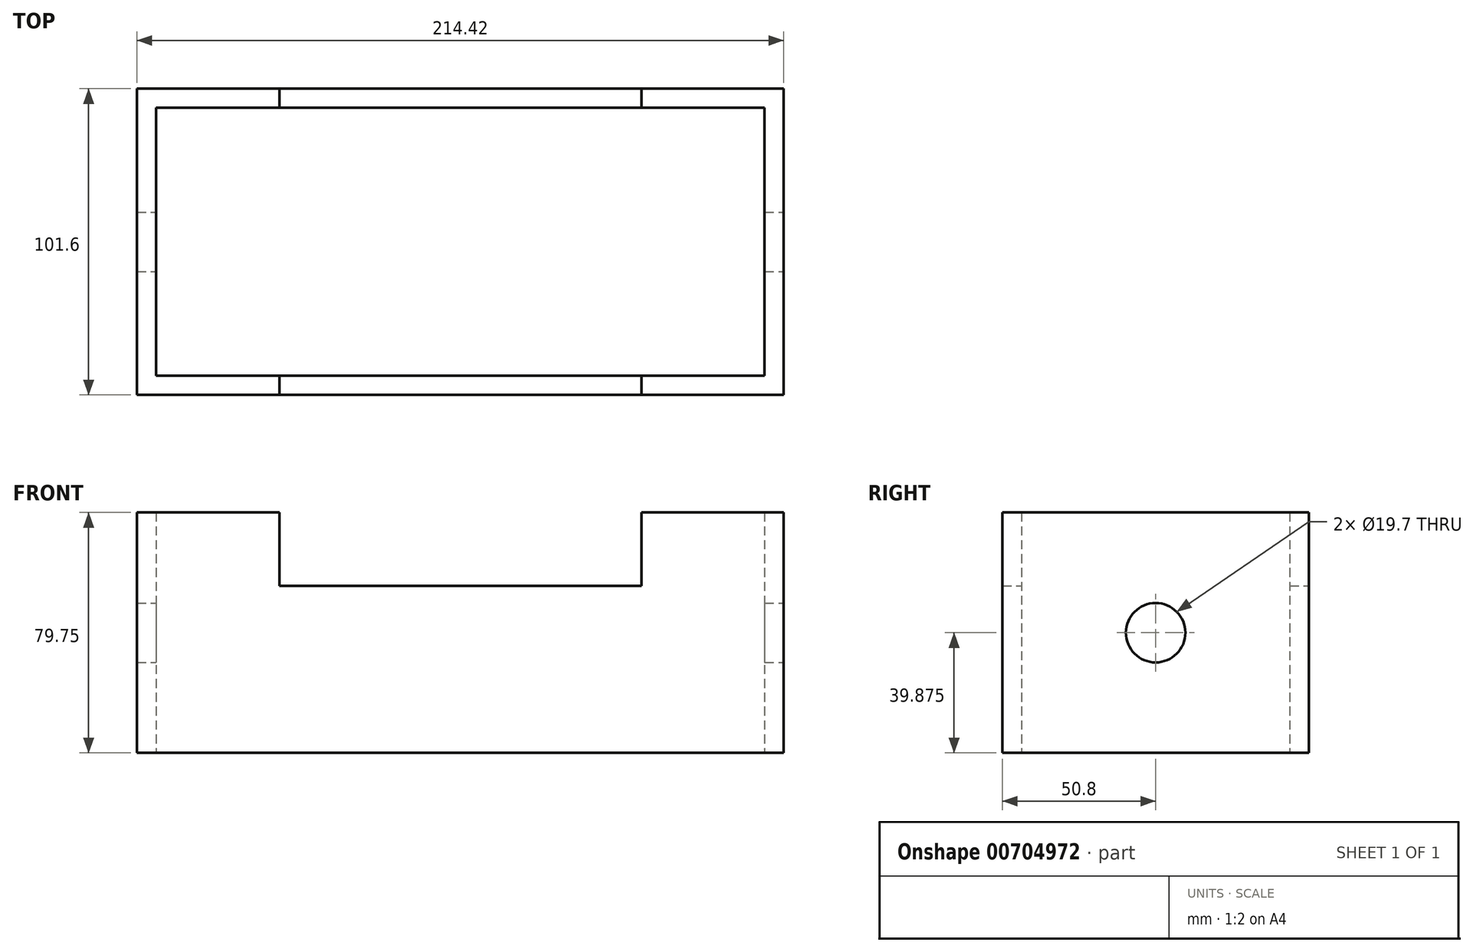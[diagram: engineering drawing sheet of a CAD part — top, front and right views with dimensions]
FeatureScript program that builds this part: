
annotation { "Feature Type Name" : "Feature", "Feature Type Description" : "" }
export const myFeature = defineFeature(function(context is Context, id is Id, definition is map)
    precondition{}
    {
        {
            var Q0;
            Q0=qCreatedBy(makeId("Front.planeOp"),FACE);
            var sketch = newSketch(context, id + "F0", { "sketchPlane" : qUnion([Q0])});
            skLineSegment(sketch, "E0", {"start": v(0, 0) * mm, "end": v(-107.21, 0) * mm});
            skLineSegment(sketch, "E1", {"start": v(-107.21, 0) * mm, "end": v(-107.21, 79.75) * mm});
            skLineSegment(sketch, "E2", {"start": v(-107.21, 79.75) * mm, "end": v(-60.03, 79.75) * mm});
            skLineSegment(sketch, "E3", {"start": v(-60.03, 79.75) * mm, "end": v(-60.03, 55.46) * mm});
            skLineSegment(sketch, "E4", {"start": v(-60.03, 55.46) * mm, "end": v(0, 55.46) * mm});
            skLineSegment(sketch, "E5.MirrorCS", {"start": v(60.03, 55.46) * mm, "end": v(0, 55.46) * mm});
            skLineSegment(sketch, "E6.MirrorCS", {"start": v(60.03, 79.75) * mm, "end": v(60.03, 55.46) * mm});
            skLineSegment(sketch, "E7.MirrorCS", {"start": v(107.21, 79.75) * mm, "end": v(60.03, 79.75) * mm});
            skLineSegment(sketch, "E8.MirrorCS", {"start": v(107.21, 0) * mm, "end": v(107.21, 79.75) * mm});
            skLineSegment(sketch, "E9.MirrorCS", {"start": v(0, 0) * mm, "end": v(107.21, 0) * mm});
            skSolve(sketch);
        }
        {
            var Q0;
            Q0=makeQuery(id+"F0.imprint","IMPRINT",FACE,{"disambiguationData":[TD([[makeQuery(id+"F0.imprint","IMPRINT",EDGE,{"derivedFrom":sQuery(id+"F0.wireOp",EDGE,"E0")}),-1.0]])]});
            extrude(context, id + "F1", {"entities" : qUnion([Q0]), "depth" : 50.8 * mm, "offsetDistance" : 25.4 * mm, "hasSecondDirection" : true, "secondDirectionOppositeDirection" : true, "secondDirectionDepth" : 50.8 * mm});
        }
        {
            var Q0;
            Q0=makeQuery(id+"F1.opExtrude","SWEPT_FACE",FACE,{"disambiguationData":[OSD([sQuery(id+"F0.wireOp",EDGE,"E8.MirrorCS")])]});
            var sketch = newSketch(context, id + "F2", { "sketchPlane" : qUnion([Q0])});
            skCircle(sketch, "E10", {"center": v(0, 39.88) * mm, "radius": 9.85 * mm});
            skPoint(sketch, "E10.centerSnap0", {"position": v(-50.8, 39.88) * mm});
            skSolve(sketch);
        }
        {
            var Q0;
            Q0 = qSketchRegion(id + "F2", true);
            extrude(context, id + "F3", {"entities" : qUnion([Q0]), "operationType" : NewBodyOperationType.REMOVE, "endBound" : BoundingType.THROUGH_ALL, "oppositeDirection" : true, "depth" : 25.4 * mm, "offsetDistance" : 25.4 * mm});
        }
        {
            var Q0;
            Q0=makeQuery(id+"F1.opExtrude","SWEPT_FACE",FACE,{"disambiguationData":[OSD([sQuery(id+"F0.wireOp",EDGE,"E0"),sQuery(id+"F0.wireOp",EDGE,"E9.MirrorCS")])]});
            var sketch = newSketch(context, id + "F4", { "sketchPlane" : qUnion([Q0])});
            skLineSegment(sketch, "E11.0", {"start": v(100.86, 44.45) * mm, "end": v(-100.86, 44.45) * mm});
            skLineSegment(sketch, "E11.1", {"start": v(100.86, 44.45) * mm, "end": v(100.86, -44.45) * mm});
            skLineSegment(sketch, "E11.2", {"start": v(100.86, -44.45) * mm, "end": v(-100.86, -44.45) * mm});
            skLineSegment(sketch, "E11.3", {"start": v(-100.86, 44.45) * mm, "end": v(-100.86, -44.45) * mm});
            skSolve(sketch);
        }
        {
            var Q0;
            Q0 = qSketchRegion(id + "F4", true);
            extrude(context, id + "F5", {"entities" : qUnion([Q0]), "operationType" : NewBodyOperationType.REMOVE, "endBound" : BoundingType.THROUGH_ALL, "oppositeDirection" : true, "depth" : 25.4 * mm, "offsetDistance" : 25.4 * mm});
        }
    });
